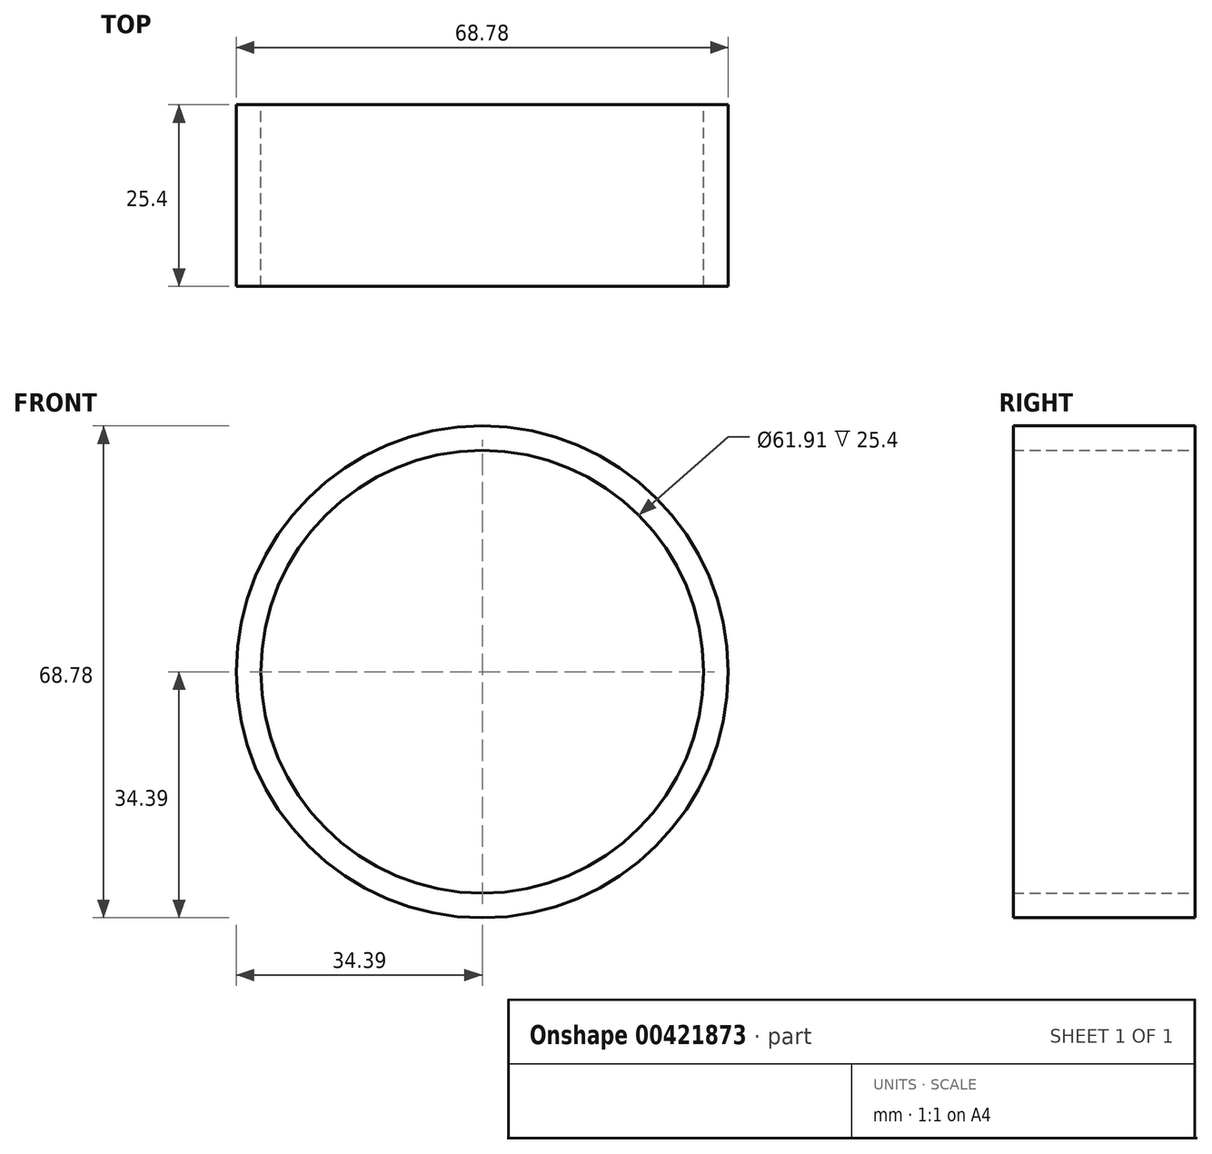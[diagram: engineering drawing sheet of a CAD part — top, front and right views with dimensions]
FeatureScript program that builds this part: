
annotation { "Feature Type Name" : "Feature", "Feature Type Description" : "" }
export const myFeature = defineFeature(function(context is Context, id is Id, definition is map)
    precondition{}
    {
        {
            var Q0;
            Q0=qCreatedBy(makeId("Front.planeOp"),FACE);
            var sketch = newSketch(context, id + "F0", { "sketchPlane" : qUnion([Q0])});
            skCircle(sketch, "E0", {"center": v(0, 0) * mm, "radius": 30.96 * mm});
            skSolve(sketch);
        }
        {
            var Q0;
            Q0=makeQuery(id+"F0.imprint","IMPRINT",FACE,{"disambiguationData":[TD([[makeQuery(id+"F0.imprint","IMPRINT",EDGE,{"derivedFrom":sQuery(id+"F0.wireOp",EDGE,"E0")}),1.0]])]});
            var sketch = newSketch(context, id + "F1", { "sketchPlane" : qUnion([Q0])});
            skCircle(sketch, "E1", {"center": v(0, 0) * mm, "radius": 34.4 * mm});
            skSolve(sketch);
        }
        {
            var Q0;
            Q0=makeQuery(id+"F1.imprint","IMPRINT",FACE,{"disambiguationData":[TD([[makeQuery(id+"F1.imprint","IMPRINT",EDGE,{"derivedFrom":sQuery(id+"F1.wireOp",EDGE,"E1")}),1.0]])]});
            extrude(context, id + "F2", {"entities" : qUnion([Q0]), "depth" : 25.4 * mm});
        }
    });
